# Revit family: highbay_21_fur_modario_r__tragschiene_midi_52hn11da5lma_a206
name_source: partatom
category: Lighting Fixtures
units: mm (PartAtom-declared; Revit-internal decimal feet)

## family parameters
Cut with Voids When Loaded = No
Host = Face
Light Source = No
Part Type = Normal
Room Calculation Point = No
Round Connector Dimension = Use Diameter
Shared = No

## types (1)
- --- (1 x LED, 4050 lm, 22.3 W, 5000K)
    Apparent Load = 22 VA
    CIE Flux Codes = 89 97 99 100 100
    Color Rendering = 80
    Color Temperature = 5000K
    Default Elevation = 1800 mm
    Description = high bay luminaire Highbay 21 for Modario® trunking rail midi; direct symmetric narrow distribution, light control with lens of PMMA; UGR ≤ 22 (X = 4H | Y = 8H | S = 0.25H | reflection values 70/50/20); luminous flux: 25.790lm; light colour: 850, colour temperature: 5000K, MacAdam ≤ 3 SDCM (initial), colour rendering: CRI > 80; luminous efficacy: 180,9lm/W; rated service life: 75.000h (L80/B50) at AT= ta max; control: DALI 2; luminaire connection: plug, 5-pole, with phase selectionmains connection: 230..240V, AC 50/60Hz; connected load: 142,6W; protection rating (complete): IP64; insulation class (complete): insulation class I (protective earthing); protection symbol: D; impact resistance: IK07; certification: CE, ENEC, VDE, UKCA; internal wiring halogen-free; luminaire corresponds to IFS (International Featured Standards) requirements for safety and quality in the food industry; LABS conformity tested according to VDMA 24364:2018-05; housing frame of high-performance plastic PA6, matt traffic white (RAL 9016); cover of PMMA; fixing on rail side of steel, galvanised, white; blank cover of PC, traffic white (RAL 9016); dimension (LxWxH): 1.195 x 442 x 72mm; permissible operating ambient temperature: -40..+55°C (reducing of maximum allowable ambient temperature of 5°C with ceiling mounting); packaging unit: 1 piece
    Height = 72 mm
    Lamp = 1 x LED
    Lamp Light Flux = 4050 lm
    Lamp Power = 22.3 W
    Lamp count = 1
    Length = 474 mm
    Luminous efficacy = 182 lm/W
    Manufacturer = Siteco
    ModVariant = No
    Model = 52HN11DA5LMA
    Mounting Place = Ceiling
    Mounting Type = Pendant
    Number of Poles = 1
    OnlyDefault = Yes
    Power Factor = 1
    Product Name = Highbay 21 für Modario® Tragschiene midi
    Product group = high bay luminaire
    ProductGroupID = 901
    Protection Class = Protection class I
    Protection Degree = IP 64
    RLX_Detail_Level = 1
    RLX_Emergency_Light_Flux = 0 lm
    RLX_Emergency_Type = 0
    RLX_Emergency_Type_DB = No
    RlxData = <blob elided: 78457 chars, md5=4042d5e7>
    Socket = socket
    Standby Power = 0 W
    System Light Flux = 4050 lm
    System Power = 22 W
    Type Comments = : DC mode (central or group accumulator) initial emergency light level
    Type Image = l_1363266.jpg
    URL = http://relux.com
    VarID = @adj_001013
    Voltage = 0 V
    Weight = 0.00 kg
    Width = 442 mm

## geometry (parser evidence)
native form markers: Sweep x10
no freeform markers — native parametric forms only
